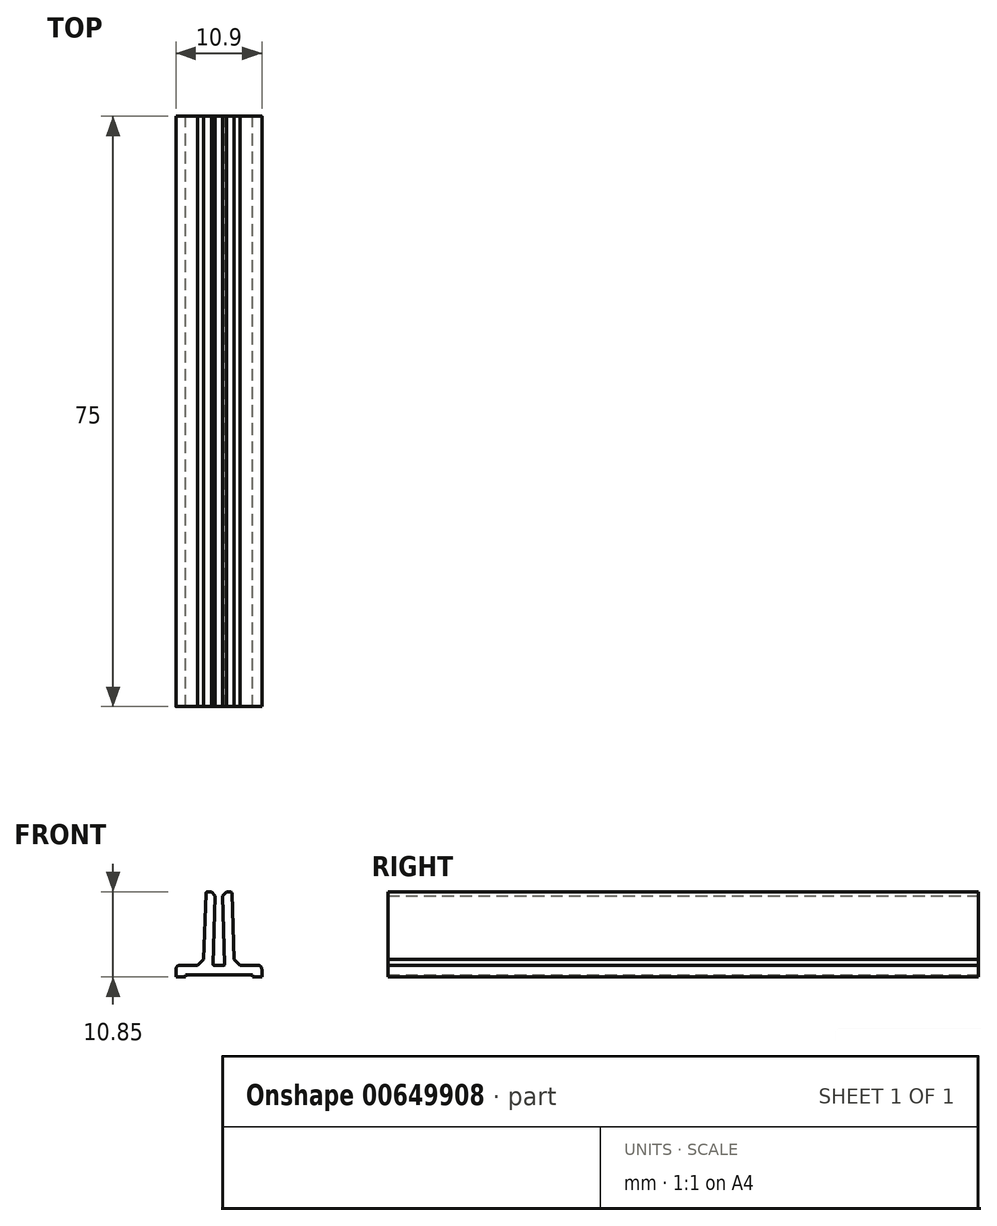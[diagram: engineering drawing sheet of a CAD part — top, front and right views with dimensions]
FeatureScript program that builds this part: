
annotation { "Feature Type Name" : "Feature", "Feature Type Description" : "" }
export const myFeature = defineFeature(function(context is Context, id is Id, definition is map)
    precondition{}
    {
        {
            var Q0;
            Q0=qCreatedBy(makeId("Front.planeOp"),FACE);
            var sketch = newSketch(context, id + "F0", { "sketchPlane" : qUnion([Q0])});
            skLineSegment(sketch, "E0.bottom", {"start": v(1.4, 5.75) * mm, "end": v(0.7, 5.75) * mm});
            skLineSegment(sketch, "E0.top", {"start": v(5.2, -5.1) * mm, "end": v(4.5, -5.1) * mm});
            skLineSegment(sketch, "E1", {"start": v(0, -3.6) * mm, "end": v(0.64, -3.6) * mm});
            skLineSegment(sketch, "E2", {"start": v(0.46, 5.5) * mm, "end": v(0.74, -3.5) * mm});
            skLineSegment(sketch, "E3", {"start": v(0.7, 5.75) * mm, "end": v(1.4, 5.75) * mm});
            skLineSegment(sketch, "E4", {"start": v(4.25, -4.8) * mm, "end": v(0, -4.8) * mm});
            skLineSegment(sketch, "E5", {"start": v(1.66, 5.5) * mm, "end": v(1.95, -3.6) * mm});
            skPoint(sketch, "E6.visualSharp", {"position": v(1.65, 5.75) * mm});
            skArc(sketch, "E6.filletArc", {"start": v(1.66, 5.5) * mm, "mid": v(1.58, 5.68) * mm, "end": v(1.4, 5.75) * mm});
            skPoint(sketch, "E7.visualSharp", {"position": v(1.95, -3.6) * mm});
            skPoint(sketch, "E8.visualSharp", {"position": v(0.75, -3.6) * mm});
            skArc(sketch, "E8.filletArc", {"start": v(0.64, -3.6) * mm, "mid": v(0.71, -3.56) * mm, "end": v(0.74, -3.5) * mm});
            skLineSegment(sketch, "E9", {"start": v(4.25, -4.8) * mm, "end": v(4.25, -5.1) * mm});
            skLineSegment(sketch, "E10", {"start": v(4.25, -5.1) * mm, "end": v(5.45, -5.1) * mm});
            skLineSegment(sketch, "E11", {"start": v(5.45, -5.1) * mm, "end": v(5.45, -4.85) * mm});
            skLineSegment(sketch, "E12", {"start": v(1.92, -2.85) * mm, "end": v(1.95, -3.6) * mm});
            skLineSegment(sketch, "E13", {"start": v(0.46, 5.5) * mm, "end": v(0.45, 5.74) * mm});
            skLineSegment(sketch, "E14", {"start": v(0.7, 5.75) * mm, "end": v(0.45, 5.74) * mm});
            skLineSegment(sketch, "E15", {"start": v(1.92, -2.85) * mm, "end": v(2.7, -3.6) * mm});
            skPoint(sketch, "E16.visualSharp", {"position": v(5.45, -3.6) * mm});
            skLineSegment(sketch, "E17", {"start": v(2.7, -3.6) * mm, "end": v(4.95, -3.6) * mm});
            skLineSegment(sketch, "E18", {"start": v(5.45, -5.1) * mm, "end": v(5.45, -4.1) * mm});
            skArc(sketch, "E19.filletArc", {"start": v(5.45, -4.1) * mm, "mid": v(5.3, -3.74) * mm, "end": v(4.95, -3.6) * mm});
            skLineSegment(sketch, "E20.MirrorCS", {"start": v(-0.46, 5.5) * mm, "end": v(-0.45, 5.74) * mm});
            skLineSegment(sketch, "E21.MirrorCS", {"start": v(-1.4, 5.75) * mm, "end": v(-0.7, 5.75) * mm});
            skLineSegment(sketch, "E22.MirrorCS", {"start": v(-0.7, 5.75) * mm, "end": v(-0.45, 5.74) * mm});
            skLineSegment(sketch, "E23.MirrorCS", {"start": v(-0.7, 5.75) * mm, "end": v(-1.4, 5.75) * mm});
            skArc(sketch, "E24.MirrorCS", {"start": v(-0.64, -3.6) * mm, "mid": v(-0.71, -3.56) * mm, "end": v(-0.74, -3.5) * mm});
            skLineSegment(sketch, "E25.MirrorCS", {"start": v(-1.92, -2.85) * mm, "end": v(-1.95, -3.6) * mm});
            skLineSegment(sketch, "E26.MirrorCS", {"start": v(-5.45, -5.1) * mm, "end": v(-5.45, -4.85) * mm});
            skArc(sketch, "E27.MirrorCS", {"start": v(-1.66, 5.5) * mm, "mid": v(-1.58, 5.68) * mm, "end": v(-1.4, 5.75) * mm});
            skLineSegment(sketch, "E28.MirrorCS", {"start": v(-5.2, -5.1) * mm, "end": v(-4.5, -5.1) * mm});
            skLineSegment(sketch, "E29.MirrorCS", {"start": v(-4.25, -4.8) * mm, "end": v(-4.25, -5.1) * mm});
            skLineSegment(sketch, "E30.MirrorCS", {"start": v(-1.92, -2.85) * mm, "end": v(-2.7, -3.6) * mm});
            skArc(sketch, "E31.MirrorCS", {"start": v(-5.45, -4.1) * mm, "mid": v(-5.3, -3.74) * mm, "end": v(-4.95, -3.6) * mm});
            skPoint(sketch, "E32.MirrorP", {"position": v(-5.45, -3.6) * mm});
            skLineSegment(sketch, "E33.MirrorCS", {"start": v(-4.25, -5.1) * mm, "end": v(-5.45, -5.1) * mm});
            skLineSegment(sketch, "E34.MirrorCS", {"start": v(-5.45, -5.1) * mm, "end": v(-5.45, -4.1) * mm});
            skLineSegment(sketch, "E35.MirrorCS", {"start": v(0, -3.6) * mm, "end": v(-0.64, -3.6) * mm});
            skPoint(sketch, "E36.MirrorP", {"position": v(-1.65, 5.75) * mm});
            skLineSegment(sketch, "E37.MirrorCS", {"start": v(-1.66, 5.5) * mm, "end": v(-1.95, -3.6) * mm});
            skPoint(sketch, "E38.MirrorP", {"position": v(-1.95, -3.6) * mm});
            skPoint(sketch, "E39.MirrorP", {"position": v(-0.75, -3.6) * mm});
            skLineSegment(sketch, "E40.MirrorCS", {"start": v(-4.25, -4.8) * mm, "end": v(0, -4.8) * mm});
            skLineSegment(sketch, "E41.MirrorCS", {"start": v(-2.7, -3.6) * mm, "end": v(-4.95, -3.6) * mm});
            skLineSegment(sketch, "E42.MirrorCS", {"start": v(-0.46, 5.5) * mm, "end": v(-0.74, -3.5) * mm});
            skSolve(sketch);
        }
        {
            var Q0;
            {var subQ4=sQuery(id+"F0.wireOp",EDGE,"E1");Q0=makeQuery(id+"F0.imprint","IMPRINT",FACE,{"disambiguationData":[TD([[makeQuery(id+"F0.imprint","IMPRINT",EDGE,{"derivedFrom":subQ4}),-1.0]])]});}
            extrude(context, id + "F1", {"entities" : qUnion([Q0]), "depth" : 75 * mm, "offsetDistance" : 25 * mm});
        }
        {
            var Q0;
            Q0=makeQuery(id+"F1.opExtrude","SWEPT_EDGE",EDGE,{"disambiguationData":[OSD([sQuery(id+"F0.wireOp",EDGE,"E20.MirrorCS"),sQuery(id+"F0.wireOp",EDGE,"E22.MirrorCS")])]});
            var Q1;
            Q1=makeQuery(id+"F1.opExtrude","SWEPT_EDGE",EDGE,{"disambiguationData":[OSD([sQuery(id+"F0.wireOp",EDGE,"E13"),sQuery(id+"F0.wireOp",EDGE,"E14")])]});
            chamfer(context, id + "F2", {"entities" : qUnion([Q0, Q1]), "width" : .5 * mm, "tangentPropagation" : true});
        }
    });
